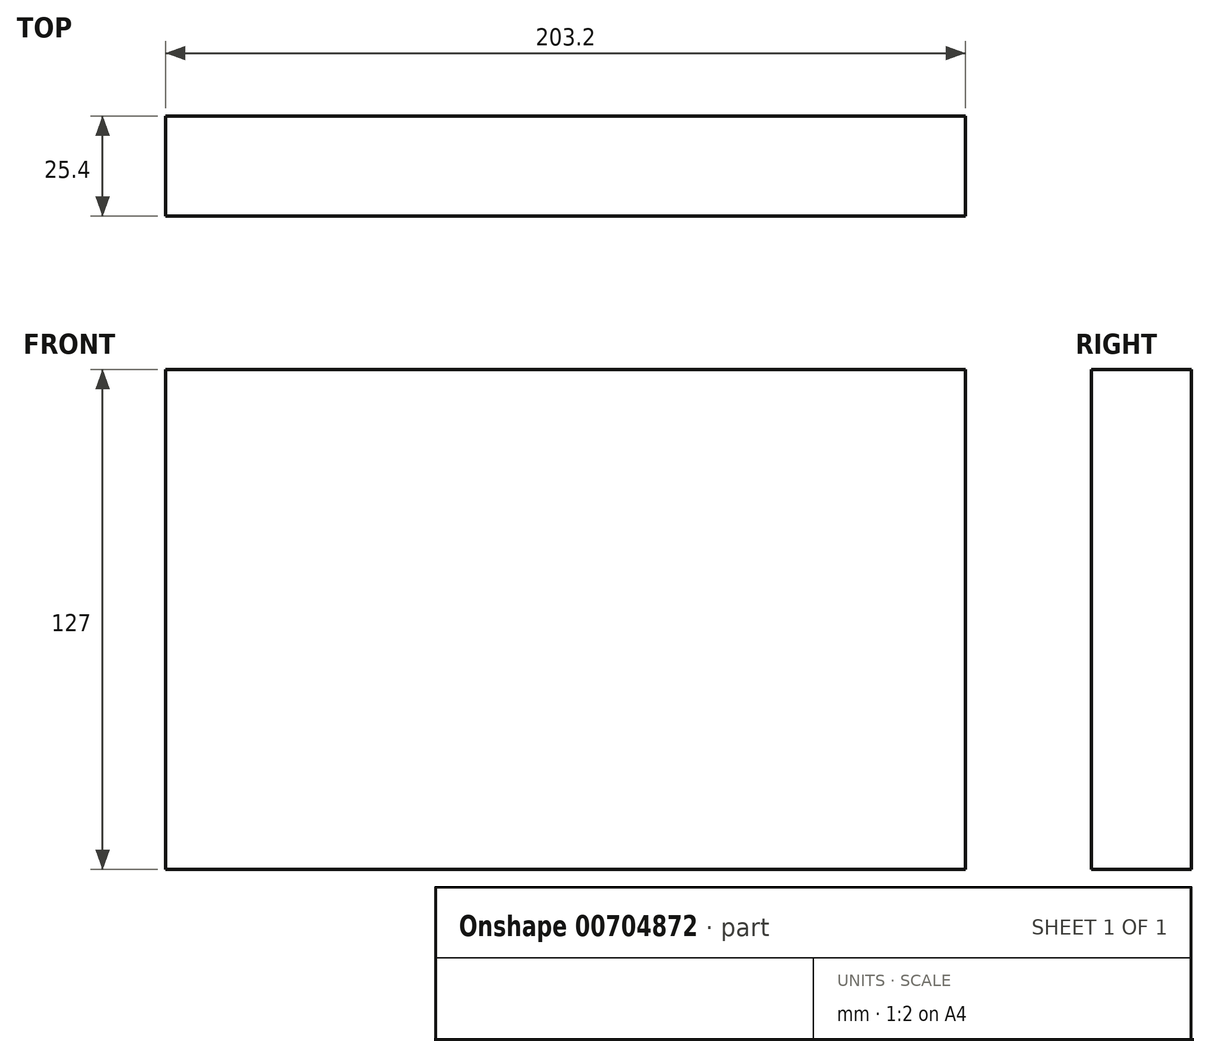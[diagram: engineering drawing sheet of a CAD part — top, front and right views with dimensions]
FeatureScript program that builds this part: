
annotation { "Feature Type Name" : "Feature", "Feature Type Description" : "" }
export const myFeature = defineFeature(function(context is Context, id is Id, definition is map)
    precondition{}
    {
        {
            var Q0;
            Q0=qCreatedBy(makeId("Front.planeOp"),FACE);
            var sketch = newSketch(context, id + "F0", { "sketchPlane" : qUnion([Q0])});
            skLineSegment(sketch, "E0.bottom", {"start": v(-61.93, 60.08) * mm, "end": v(141.27, 60.08) * mm});
            skLineSegment(sketch, "E0.top", {"start": v(-61.93, -66.92) * mm, "end": v(141.27, -66.92) * mm});
            skLineSegment(sketch, "E0.left", {"start": v(-61.93, 60.08) * mm, "end": v(-61.93, -66.92) * mm});
            skLineSegment(sketch, "E0.right", {"start": v(141.27, 60.08) * mm, "end": v(141.27, -66.92) * mm});
            skSolve(sketch);
        }
        {
            var Q0;
            Q0=makeQuery(id+"F0.imprint","IMPRINT",FACE,{"disambiguationData":[TD([[makeQuery(id+"F0.imprint","IMPRINT",EDGE,{"derivedFrom":sQuery(id+"F0.wireOp",EDGE,"E0.bottom")}),-1.0]])]});
            extrude(context, id + "F1", {"entities" : qUnion([Q0]), "depth" : 25.4 * mm, "offsetDistance" : 25.4 * mm});
        }
    });
